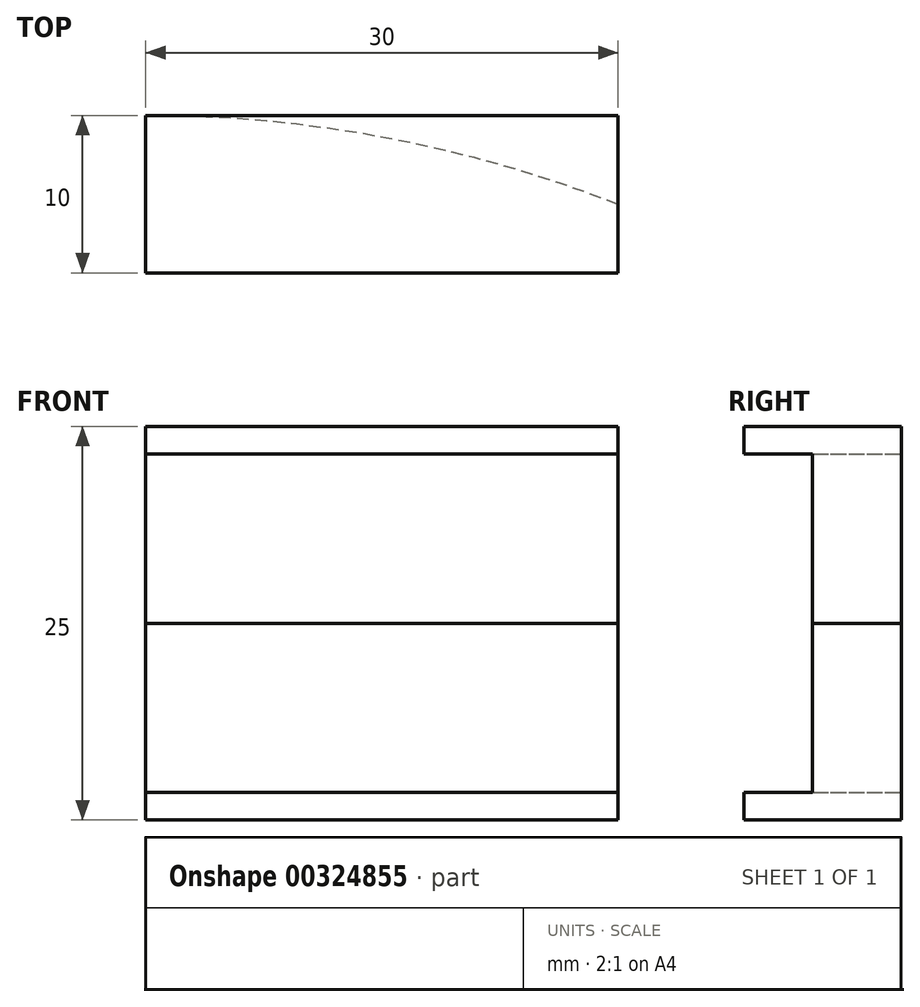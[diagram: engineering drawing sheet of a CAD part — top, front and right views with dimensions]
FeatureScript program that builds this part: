
annotation { "Feature Type Name" : "Feature", "Feature Type Description" : "" }
export const myFeature = defineFeature(function(context is Context, id is Id, definition is map)
    precondition{}
    {
        {
            assignVariable(context, id + "F0", {"name" : "RollSideWallWidth", "anyValue" : 5});
        }
        {
            var Q0;
            Q0=qCreatedBy(makeId("Top.planeOp"),FACE);
            var sketch = newSketch(context, id + "F1", { "sketchPlane" : qUnion([Q0])});
            skLineSegment(sketch, "E0.bottom", {"start": v(30, 0) * mm, "end": v(0, 0) * mm});
            skLineSegment(sketch, "E0.top", {"start": v(30, -10) * mm, "end": v(0, -10) * mm});
            skLineSegment(sketch, "E0.left", {"start": v(0, -10) * mm, "end": v(0, 0) * mm});
            skLineSegment(sketch, "E0.right", {"start": v(30, -10) * mm, "end": v(30, 0) * mm});
            skSolve(sketch);
        }
        {
            var Q0;
            Q0 = qSketchRegion(id + "F1", true);
            extrude(context, id + "F2", {"entities" : qUnion([Q0]), "depth" : (getVariable(context, 'RollSideWallWidth') * 2.5) * mm});
        }
        {
            var Q0;
            Q0=makeQuery(id+"F2.opExtrude","CAP_FACE",FACE,{"disambiguationData":[OSD([sQuery(id+"F1.wireOp",EDGE,"E0.bottom"),sQuery(id+"F1.wireOp",EDGE,"E0.top"),sQuery(id+"F1.wireOp",EDGE,"E0.left"),sQuery(id+"F1.wireOp",EDGE,"E0.right")])],"isStart":false});
            var sketch = newSketch(context, id + "F3", { "sketchPlane" : qUnion([Q0])});
            skArc(sketch, "E1", {"start": v(30, -5.65) * mm, "mid": v(15.26, -1.42) * mm, "end": v(0, 0) * mm});
            skLineSegment(sketch, "E2.0", {"start": v(30, 0) * mm, "end": v(0, 0) * mm, "construction": true});
            skLineSegment(sketch, "E3.0", {"start": v(0, -10) * mm, "end": v(0, 0) * mm});
            skLineSegment(sketch, "E3.1", {"start": v(30, -10) * mm, "end": v(0, -10) * mm});
            skLineSegment(sketch, "E4", {"start": v(30, -10) * mm, "end": v(30, -5.65) * mm});
            skSolve(sketch);
        }
        {
            var Q0;
            Q0 = qSketchRegion(id + "F3", true);
            var Q1;
            {var subQ0=sQuery(id+"F3.wireOp",EDGE,"T5neUL7d-Px9Z-BZtc-PV0f-OhhonrqpmqeQ");Q1=makeQuery(id+"F3.imprint","IMPRINT",FACE,{"disambiguationData":[TD([[makeQuery(id+"F3.imprint","IMPRINT",EDGE,{"derivedFrom":subQ0}),1.0]])]});}
            extrude(context, id + "F4", {"entities" : qUnion([Q0, Q1]), "operationType" : NewBodyOperationType.REMOVE, "oppositeDirection" : true, "depth" : (getVariable(context, 'RollSideWallWidth') * 2.15) * mm});
        }
        {
            var Q0;
            Q0=makeQuery(id+"F2.opExtrude","SWEPT_BODY",BODY,{"disambiguationData":[OSD([sQuery(id+"F1.wireOp",EDGE,"E0.bottom"),sQuery(id+"F1.wireOp",EDGE,"E0.top"),sQuery(id+"F1.wireOp",EDGE,"E0.left"),sQuery(id+"F1.wireOp",EDGE,"E0.right")])]});
            var Q1;
            Q1=makeQuery(id+"F2.opExtrude","CAP_FACE",FACE,{"disambiguationData":[OSD([sQuery(id+"F1.wireOp",EDGE,"E0.bottom"),sQuery(id+"F1.wireOp",EDGE,"E0.top"),sQuery(id+"F1.wireOp",EDGE,"E0.left"),sQuery(id+"F1.wireOp",EDGE,"E0.right")])],"isStart":false});
            mirror(context, id + "F5", {"entities" : qUnion([Q0]), "mirrorPlane" : qUnion([Q1])});
        }
    });
